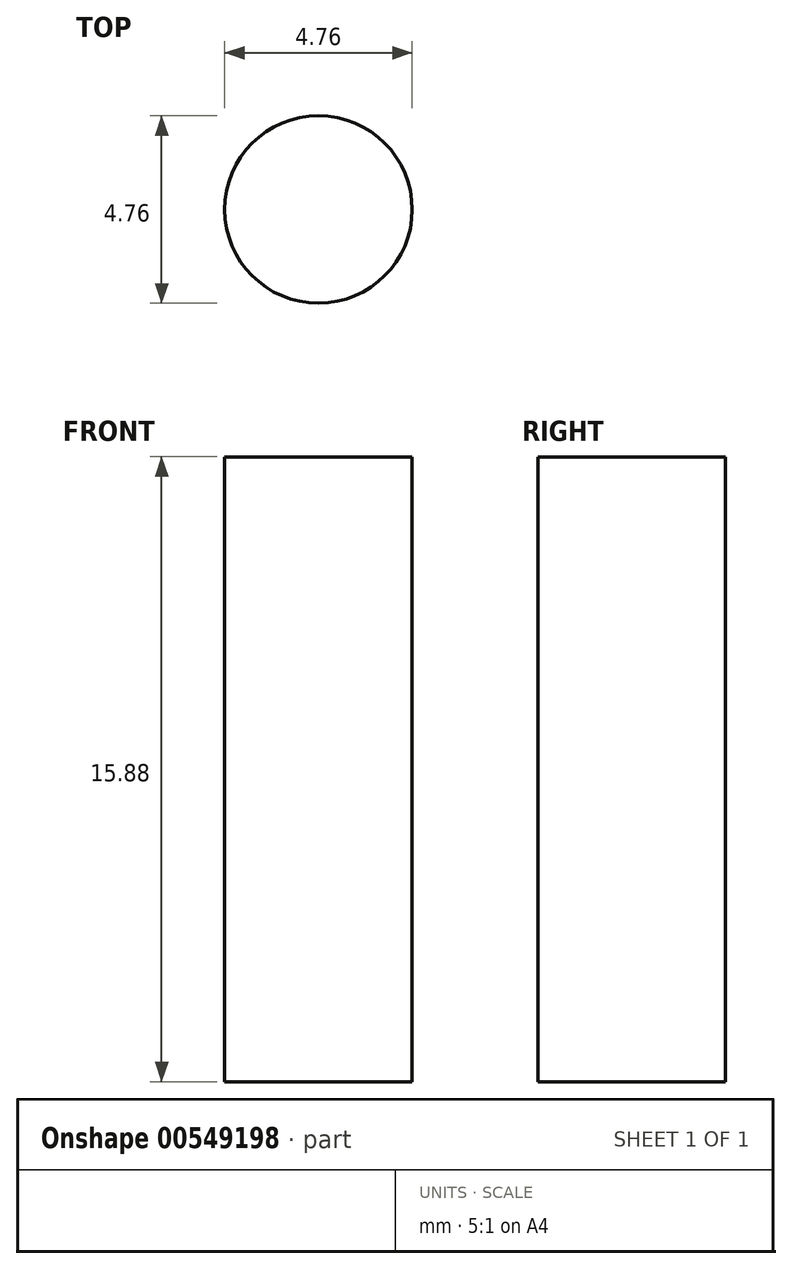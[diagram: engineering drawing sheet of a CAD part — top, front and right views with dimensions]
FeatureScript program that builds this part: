
annotation { "Feature Type Name" : "Feature", "Feature Type Description" : "" }
export const myFeature = defineFeature(function(context is Context, id is Id, definition is map)
    precondition{}
    {
        {
            var Q0;
            Q0=qCreatedBy(makeId("Top.planeOp"),FACE);
            var sketch = newSketch(context, id + "F0", { "sketchPlane" : qUnion([Q0])});
            skCircle(sketch, "E0", {"center": v(0, 0) * mm, "radius": 2.38 * mm});
            skSolve(sketch);
        }
        {
            var Q0;
            Q0=makeQuery(id+"F0.imprint","IMPRINT",FACE,{"disambiguationData":[TD([[makeQuery(id+"F0.imprint","IMPRINT",EDGE,{"derivedFrom":sQuery(id+"F0.wireOp",EDGE,"E0")}),1.0]])]});
            extrude(context, id + "F1", {"entities" : qUnion([Q0]), "depth" : 15.88 * mm, "offsetDistance" : 25.4 * mm});
        }
    });
